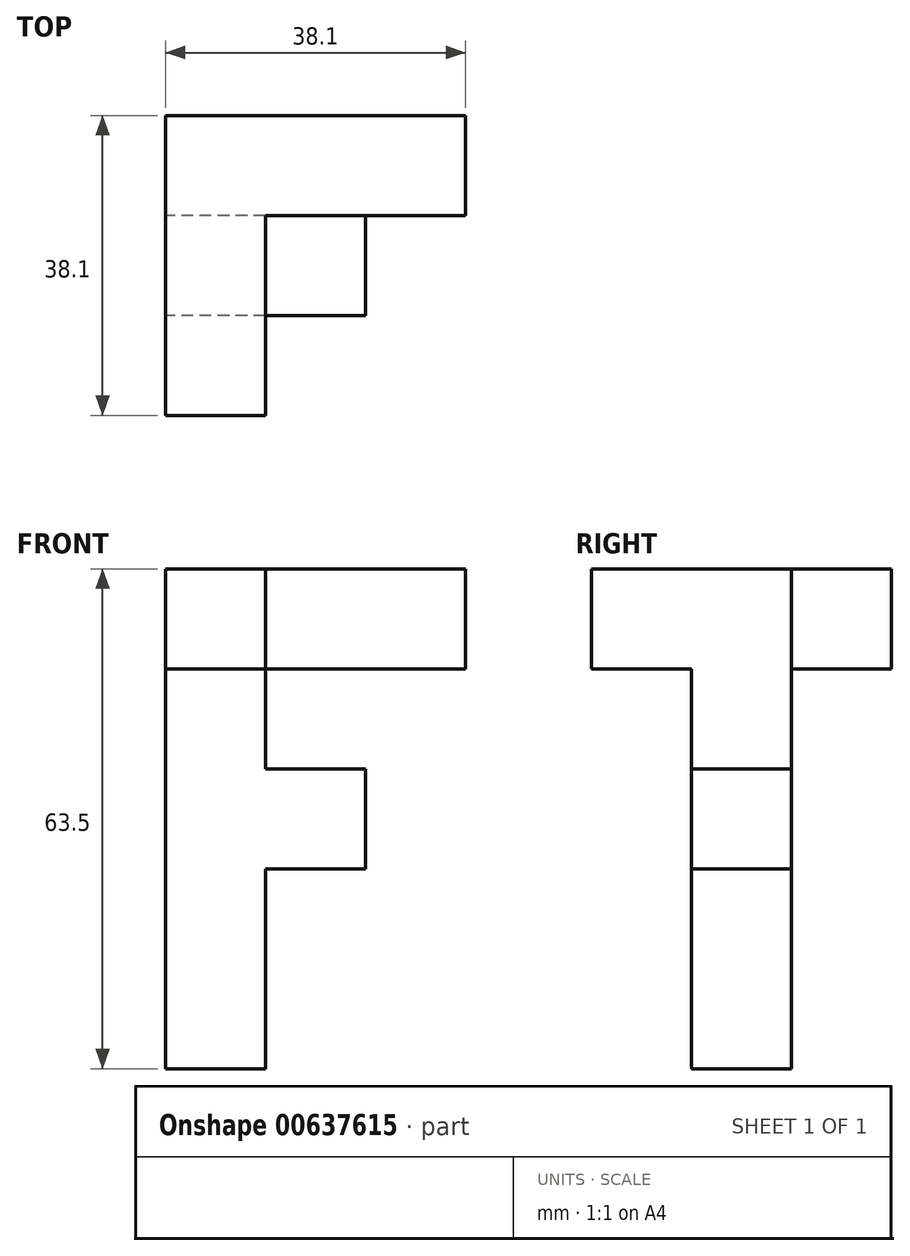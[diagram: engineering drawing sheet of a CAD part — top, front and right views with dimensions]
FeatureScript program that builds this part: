
annotation { "Feature Type Name" : "Feature", "Feature Type Description" : "" }
export const myFeature = defineFeature(function(context is Context, id is Id, definition is map)
    precondition{}
    {
        {
            var Q0;
            Q0=qCreatedBy(makeId("Front.planeOp"),FACE);
            var sketch = newSketch(context, id + "F0", { "sketchPlane" : qUnion([Q0])});
            skLineSegment(sketch, "E0.bottom", {"start": v(0, 0) * mm, "end": v(12.7, 0) * mm});
            skLineSegment(sketch, "E0.top", {"start": v(0, 63.5) * mm, "end": v(12.7, 63.5) * mm});
            skLineSegment(sketch, "E0.left", {"start": v(0, 0) * mm, "end": v(0, 63.5) * mm});
            skLineSegment(sketch, "E0.right", {"start": v(12.7, 0) * mm, "end": v(12.7, 63.5) * mm});
            skLineSegment(sketch, "E1.bottom", {"start": v(12.7, 38.1) * mm, "end": v(25.4, 38.1) * mm});
            skLineSegment(sketch, "E1.top", {"start": v(12.7, 25.4) * mm, "end": v(25.4, 25.4) * mm});
            skLineSegment(sketch, "E1.left", {"start": v(12.7, 38.1) * mm, "end": v(12.7, 25.4) * mm});
            skLineSegment(sketch, "E1.right", {"start": v(25.4, 38.1) * mm, "end": v(25.4, 25.4) * mm});
            skSolve(sketch);
        }
        {
            var Q0;
            Q0 = qSketchRegion(id + "F0", true);
            extrude(context, id + "F1", {"entities" : qUnion([Q0]), "depth" : 12.7 * mm, "offsetDistance" : 25.4 * mm});
        }
        {
            var Q0;
            Q0=makeQuery(id+"F1.opExtrude","CAP_FACE",FACE,{"disambiguationData":[OSD([sQuery(id+"F0.wireOp",EDGE,"E0.bottom"),sQuery(id+"F0.wireOp",EDGE,"E0.top"),sQuery(id+"F0.wireOp",EDGE,"E0.left"),sQuery(id+"F0.wireOp",EDGE,"E0.right"),sQuery(id+"F0.wireOp",EDGE,"E1.bottom"),sQuery(id+"F0.wireOp",EDGE,"E1.top"),sQuery(id+"F0.wireOp",EDGE,"E1.right")])],"isStart":false});
            var sketch = newSketch(context, id + "F2", { "sketchPlane" : qUnion([Q0])});
            skLineSegment(sketch, "E2.bottom", {"start": v(0, 63.5) * mm, "end": v(12.7, 63.5) * mm});
            skLineSegment(sketch, "E2.top", {"start": v(0, 50.8) * mm, "end": v(12.7, 50.8) * mm});
            skLineSegment(sketch, "E2.left", {"start": v(0, 63.5) * mm, "end": v(0, 50.8) * mm});
            skLineSegment(sketch, "E2.right", {"start": v(12.7, 63.5) * mm, "end": v(12.7, 50.8) * mm});
            skSolve(sketch);
        }
        {
            var Q0;
            Q0 = qSketchRegion(id + "F2", true);
            extrude(context, id + "F3", {"entities" : qUnion([Q0]), "operationType" : NewBodyOperationType.ADD, "depth" : 12.7 * mm, "offsetDistance" : 25.4 * mm, "hasSecondDirection" : true, "secondDirectionOppositeDirection" : true, "secondDirectionDepth" : 25.4 * mm});
        }
        {
            var Q0;
            {var subQ0=sQuery(id+"F0.wireOp",EDGE,"E0.right");Q0=makeQuery(id+"F3.boolean.opBoolean","MERGE",FACE,{"derivedFrom":[makeQuery(id+"F1.opExtrude","SWEPT_FACE",FACE,{"disambiguationData":[OSD([subQ0]),TDD([makeQuery(id+"F0.imprint","IMPRINT",EDGE,{"disambiguationData":[TD([[makeQuery(id+"F0.imprint","INTERSECT",VERTEX,{"derivedFrom":[sQuery(id+"F0.wireOp",EDGE,"E0.top"),subQ0]}),1.0]])],"derivedFrom":subQ0})])]}),makeQuery(id+"F3.opExtrude","SWEPT_FACE",FACE,{"disambiguationData":[OSD([sQuery(id+"F2.wireOp",EDGE,"E2.right")])]})]});}
            var sketch = newSketch(context, id + "F4", { "sketchPlane" : qUnion([Q0])});
            skLineSegment(sketch, "E3.bottom", {"start": v(12.7, 63.5) * mm, "end": v(0, 63.5) * mm});
            skLineSegment(sketch, "E3.top", {"start": v(12.7, 50.8) * mm, "end": v(0, 50.8) * mm});
            skLineSegment(sketch, "E3.left", {"start": v(12.7, 63.5) * mm, "end": v(12.7, 50.8) * mm});
            skLineSegment(sketch, "E3.right", {"start": v(0, 63.5) * mm, "end": v(0, 50.8) * mm});
            skSolve(sketch);
        }
        {
            var Q0;
            Q0 = qSketchRegion(id + "F4", true);
            extrude(context, id + "F5", {"entities" : qUnion([Q0]), "operationType" : NewBodyOperationType.ADD, "depth" : 25.4 * mm, "offsetDistance" : 25.4 * mm});
        }
    });
